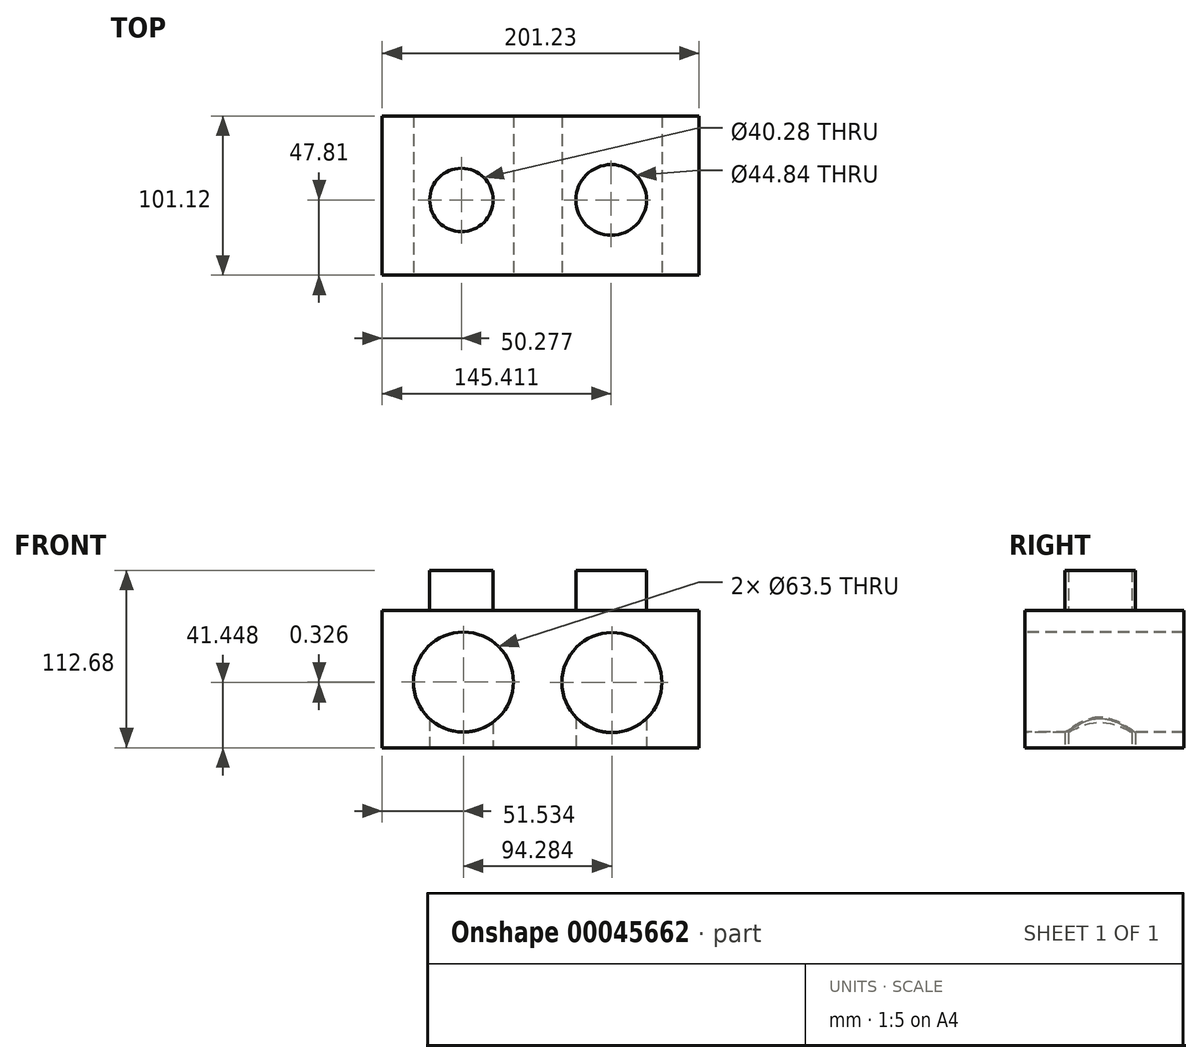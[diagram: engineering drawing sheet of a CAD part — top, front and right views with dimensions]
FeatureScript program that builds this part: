
annotation { "Feature Type Name" : "Feature", "Feature Type Description" : "" }
export const myFeature = defineFeature(function(context is Context, id is Id, definition is map)
    precondition{}
    {
        {
            var Q0;
            Q0=qCreatedBy(makeId("Top.planeOp"),FACE);
            var sketch = newSketch(context, id + "F0", { "sketchPlane" : qUnion([Q0])});
            skLineSegment(sketch, "E0.bottom", {"start": v(-73.45, 53.31) * mm, "end": v(67.83, 53.31) * mm});
            skLineSegment(sketch, "E0.top", {"start": v(-73.45, -47.81) * mm, "end": v(67.83, -47.81) * mm});
            skLineSegment(sketch, "E0.left", {"start": v(-73.45, 53.31) * mm, "end": v(-73.45, -47.81) * mm});
            skLineSegment(sketch, "E0.right", {"start": v(67.83, 53.31) * mm, "end": v(67.83, -47.81) * mm});
            skSolve(sketch);
        }
        {
            var Q0;
            Q0=makeQuery(id+"F0.imprint","IMPRINT",FACE,{"disambiguationData":[TD([[makeQuery(id+"F0.imprint","IMPRINT",EDGE,{"derivedFrom":sQuery(id+"F0.wireOp",EDGE,"E0.bottom")}),-1.0]])]});
            extrude(context, id + "F1", {"entities" : qUnion([Q0]), "depth" : 87.28 * mm});
        }
        {
            var Q0;
            Q0=makeQuery(id+"F1.opExtrude","SWEPT_FACE",FACE,{"disambiguationData":[OSD([sQuery(id+"F0.wireOp",EDGE,"E0.left")])]});
            extrude(context, id + "F2", {"entities" : qUnion([Q0]), "operationType" : NewBodyOperationType.ADD, "depth" : 59.96 * mm});
        }
        {
            var Q0;
            {var subQ0=sQuery(id+"F0.wireOp",EDGE,"E0.left");Q0=makeQuery(id+"F2.boolean.opBoolean","MERGE",FACE,{"derivedFrom":[makeQuery(id+"F1.opExtrude","CAP_FACE",FACE,{"disambiguationData":[OSD([sQuery(id+"F0.wireOp",EDGE,"E0.bottom"),sQuery(id+"F0.wireOp",EDGE,"E0.top"),subQ0,sQuery(id+"F0.wireOp",EDGE,"E0.right")])],"isStart":false}),makeQuery(id+"F2.opExtrude","SWEPT_FACE",FACE,{"disambiguationData":[OSD([subQ0]),TDD([makeQuery(id+"F1.opExtrude","CAP_EDGE",EDGE,{"disambiguationData":[OSD([subQ0])],"isStart":false})])]})]});}
            var sketch = newSketch(context, id + "F3", { "sketchPlane" : qUnion([Q0])});
            skCircle(sketch, "E1", {"center": v(-83.12, 0) * mm, "radius": 20.14 * mm});
            skSolve(sketch);
        }
        {
            var Q0;
            Q0=makeQuery(id+"F3.imprint","IMPRINT",FACE,{"disambiguationData":[TD([[makeQuery(id+"F3.imprint","IMPRINT",EDGE,{"derivedFrom":sQuery(id+"F3.wireOp",EDGE,"E1")}),-1.0]])]});
            var sketch = newSketch(context, id + "F4", { "sketchPlane" : qUnion([Q0])});
            skCircle(sketch, "E2", {"center": v(12.01, 0) * mm, "radius": 22.42 * mm});
            skSolve(sketch);
        }
        {
            var Q0;
            Q0=makeQuery(id+"F4.imprint","IMPRINT",FACE,{"disambiguationData":[TD([[makeQuery(id+"F4.imprint","IMPRINT",EDGE,{"derivedFrom":sQuery(id+"F4.wireOp",EDGE,"E2")}),1.0]])]});
            extrude(context, id + "F5", {"entities" : qUnion([Q0]), "operationType" : NewBodyOperationType.ADD, "depth" : 25.4 * mm});
        }
        {
            var Q0;
            Q0=makeQuery(id+"F3.imprint","IMPRINT",FACE,{"disambiguationData":[TD([[makeQuery(id+"F3.imprint","IMPRINT",EDGE,{"derivedFrom":sQuery(id+"F3.wireOp",EDGE,"E1")}),1.0]])]});
            extrude(context, id + "F6", {"entities" : qUnion([Q0]), "operationType" : NewBodyOperationType.ADD, "depth" : 25.4 * mm});
        }
        {
            var Q0;
            Q0=makeQuery(id+"F5.opExtrude","CAP_FACE",FACE,{"disambiguationData":[OSD([sQuery(id+"F4.wireOp",EDGE,"E2")])],"isStart":false});
            extrude(context, id + "F7", {"entities" : qUnion([Q0]), "operationType" : NewBodyOperationType.ADD, "oppositeDirection" : true, "depth" : 164.36 * mm});
        }
        {
            var Q0;
            Q0=makeQuery(id+"F6.opExtrude","CAP_FACE",FACE,{"disambiguationData":[OSD([sQuery(id+"F3.wireOp",EDGE,"E1")])],"isStart":false});
            extrude(context, id + "F8", {"entities" : qUnion([Q0]), "operationType" : NewBodyOperationType.ADD, "oppositeDirection" : true, "depth" : 163.52 * mm});
        }
        {
            var Q0;
            Q0=makeQuery(id+"F8.opExtrude","CAP_FACE",FACE,{"disambiguationData":[OSD([sQuery(id+"F3.wireOp",EDGE,"E1")])],"isStart":false});
            extrude(context, id + "F9", {"entities" : qUnion([Q0]), "operationType" : NewBodyOperationType.REMOVE, "oppositeDirection" : true, "depth" : 63.5 * mm});
        }
        {
            var Q0;
            Q0=makeQuery(id+"F7.opExtrude","CAP_FACE",FACE,{"disambiguationData":[OSD([sQuery(id+"F4.wireOp",EDGE,"E2")])],"isStart":false});
            extrude(context, id + "F10", {"entities" : qUnion([Q0]), "operationType" : NewBodyOperationType.REMOVE, "oppositeDirection" : true, "depth" : 63.5 * mm});
        }
        {
            var Q0;
            Q0=makeQuery(id+"F9.boolean.opBoolean","COPY",FACE,{"derivedFrom":makeQuery(id+"F9.opExtrude","CAP_FACE",FACE,{"disambiguationData":[OSD([sQuery(id+"F3.wireOp",EDGE,"E1")])],"isStart":false})});
            extrude(context, id + "F11", {"entities" : qUnion([Q0]), "operationType" : NewBodyOperationType.REMOVE, "oppositeDirection" : true, "depth" : 25.4 * mm});
        }
        {
            var Q0;
            Q0=makeQuery(id+"F10.boolean.opBoolean","COPY",FACE,{"derivedFrom":makeQuery(id+"F10.opExtrude","CAP_FACE",FACE,{"disambiguationData":[OSD([sQuery(id+"F4.wireOp",EDGE,"E2")])],"isStart":false})});
            extrude(context, id + "F12", {"entities" : qUnion([Q0]), "operationType" : NewBodyOperationType.REMOVE, "oppositeDirection" : true, "depth" : 25.4 * mm});
        }
        {
            var Q0;
            {var subQ0=sQuery(id+"F0.wireOp",EDGE,"E0.top");Q0=makeQuery(id+"F2.boolean.opBoolean","MERGE",FACE,{"derivedFrom":[makeQuery(id+"F1.opExtrude","SWEPT_FACE",FACE,{"disambiguationData":[OSD([subQ0])]}),makeQuery(id+"F2.opExtrude","SWEPT_FACE",FACE,{"disambiguationData":[OSD([subQ0,sQuery(id+"F0.wireOp",EDGE,"E0.left")])]})]});}
            var sketch = newSketch(context, id + "F13", { "sketchPlane" : qUnion([Q0])});
            skCircle(sketch, "E3", {"center": v(-85.99, 47.9) * mm, "radius": 31 * mm});
            skCircle(sketch, "E4", {"center": v(12.42, 41.45) * mm, "radius": 31.32 * mm});
            skSolve(sketch);
        }
        {
            var Q0;
            Q0=sQuery(id+"F13.wireOp",VERTEX,"E4.center");
            var Q1;
            Q1=makeQuery(id+"F1.opExtrude","SWEPT_BODY",BODY,{"disambiguationData":[OSD([sQuery(id+"F0.wireOp",EDGE,"E0.bottom"),sQuery(id+"F0.wireOp",EDGE,"E0.top"),sQuery(id+"F0.wireOp",EDGE,"E0.left"),sQuery(id+"F0.wireOp",EDGE,"E0.right")])]});
            hole(context, id + "F14", {"style" : HoleStyle.SIMPLE, "holeDiameter" : 63.5 * mm, "endStyle" : HoleEndStyle.THROUGH, "locations" : qUnion([Q0]), "scope" : qUnion([Q1])});
        }
        {
            var Q0;
            {var subQ0=sQuery(id+"F0.wireOp",EDGE,"E0.top");Q0=makeQuery(id+"F2.boolean.opBoolean","MERGE",FACE,{"derivedFrom":[makeQuery(id+"F1.opExtrude","SWEPT_FACE",FACE,{"disambiguationData":[OSD([subQ0])]}),makeQuery(id+"F2.opExtrude","SWEPT_FACE",FACE,{"disambiguationData":[OSD([subQ0,sQuery(id+"F0.wireOp",EDGE,"E0.left")])]})]});}
            var sketch = newSketch(context, id + "F15", { "sketchPlane" : qUnion([Q0])});
            skSolve(sketch);
        }
        {
            var Q0;
            {var subQ1=sQuery(id+"F0.wireOp",EDGE,"E0.top");Q0=makeQuery(id+"F15.imprint","IMPRINT",FACE,{"disambiguationData":[TD([[makeQuery(id+"F15.imprint","IMPRINT",EDGE,{"derivedFrom":makeQuery(id+"F1.opExtrude","SWEPT_EDGE",EDGE,{"disambiguationData":[OSD([subQ1,sQuery(id+"F0.wireOp",EDGE,"E0.right")])]})}),-1.0]])]});}
            var sketch = newSketch(context, id + "F16", { "sketchPlane" : qUnion([Q0])});
            skCircle(sketch, "E5", {"center": v(-81.87, 41.77) * mm, "radius": 32.64 * mm});
            skSolve(sketch);
        }
        {
            var Q0;
            Q0=sQuery(id+"F16.wireOp",VERTEX,"E5.center");
            var Q1;
            Q1=makeQuery(id+"F1.opExtrude","SWEPT_BODY",BODY,{"disambiguationData":[OSD([sQuery(id+"F0.wireOp",EDGE,"E0.bottom"),sQuery(id+"F0.wireOp",EDGE,"E0.top"),sQuery(id+"F0.wireOp",EDGE,"E0.left"),sQuery(id+"F0.wireOp",EDGE,"E0.right")])]});
            hole(context, id + "F17", {"style" : HoleStyle.SIMPLE, "holeDiameter" : 63.5 * mm, "endStyle" : HoleEndStyle.THROUGH, "locations" : qUnion([Q0]), "scope" : qUnion([Q1])});
        }
    });
